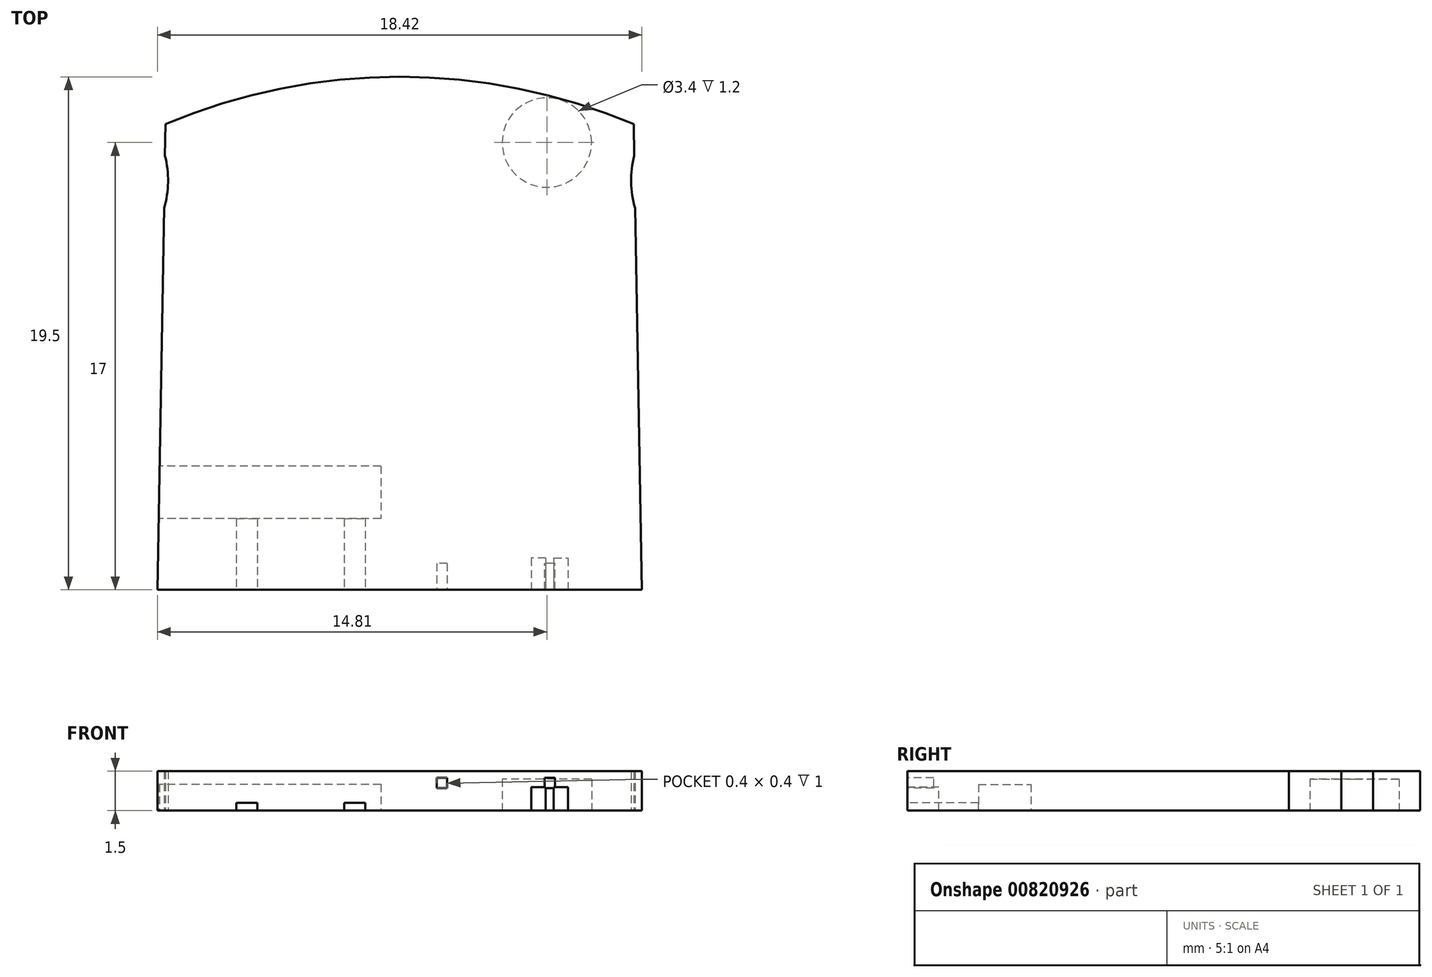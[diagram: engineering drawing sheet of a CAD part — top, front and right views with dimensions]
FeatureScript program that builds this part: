
annotation { "Feature Type Name" : "Feature", "Feature Type Description" : "" }
export const myFeature = defineFeature(function(context is Context, id is Id, definition is map)
    precondition{}
    {
        {
            var Q0;
            Q0=qCreatedBy(makeId("Top.planeOp"),FACE);
            var sketch = newSketch(context, id + "F0", { "sketchPlane" : qUnion([Q0])});
            skLineSegment(sketch, "E0", {"start": v(-9.2, 0) * mm, "end": v(9.21, 0) * mm});
            skLineSegment(sketch, "E1", {"start": v(-9.21, 0) * mm, "end": v(-8.9, 17.7) * mm});
            skLineSegment(sketch, "E2", {"start": v(-8.9, 17.7) * mm, "end": v(8.9, 17.7) * mm});
            skLineSegment(sketch, "E3", {"start": v(8.9, 17.7) * mm, "end": v(9.21, 0) * mm});
            skPoint(sketch, "E4", {"position": v(0, 19.5) * mm});
            skArc(sketch, "E5", {"start": v(8.9, 17.7) * mm, "mid": v(0, 19.5) * mm, "end": v(-8.9, 17.7) * mm});
            skPoint(sketch, "E6", {"position": v(-8.96, 14.5) * mm});
            skPoint(sketch, "E7", {"position": v(-8.92, 16.5) * mm});
            skPoint(sketch, "E8", {"position": v(-8.8, 15.5) * mm});
            skArc(sketch, "E9", {"start": v(-8.96, 14.5) * mm, "mid": v(-8.8, 15.5) * mm, "end": v(-8.92, 16.5) * mm});
            skArc(sketch, "E10.MirrorCS", {"start": v(8.96, 14.5) * mm, "mid": v(8.8, 15.5) * mm, "end": v(8.92, 16.5) * mm});
            skSolve(sketch);
        }
        {
            var Q0;
            {var subQ4=sQuery(id+"F0.wireOp",EDGE,"E0");Q0=makeQuery(id+"F0.imprint","IMPRINT",FACE,{"disambiguationData":[TD([[makeQuery(id+"F0.imprint","IMPRINT",EDGE,{"derivedFrom":subQ4}),1.0]])]});}
            var Q1;
            Q1=makeQuery(id+"F0.imprint","IMPRINT",FACE,{"disambiguationData":[TD([[makeQuery(id+"F0.imprint","IMPRINT",EDGE,{"derivedFrom":sQuery(id+"F0.wireOp",EDGE,"E2")}),1.0]])]});
            extrude(context, id + "F1", {"entities" : qUnion([Q0, Q1]), "depth" : 1.5 * mm, "offsetDistance" : 25 * mm});
        }
        {
            var Q0;
            Q0=qCreatedBy(makeId("Top.planeOp"),FACE);
            var sketch = newSketch(context, id + "F2", { "sketchPlane" : qUnion([Q0])});
            skLineSegment(sketch, "E11", {"start": v(5.6, 21.02) * mm, "end": v(5.6, -2.21) * mm, "construction": true});
            skLineSegment(sketch, "E12", {"start": v(13.66, 17) * mm, "end": v(-14.4, 17) * mm, "construction": true});
            skCircle(sketch, "E13", {"center": v(5.6, 17) * mm, "radius": 1.7 * mm});
            skCircle(sketch, "E14.MirrorC", {"center": v(-5.6, 17) * mm, "radius": 1.7 * mm});
            skSolve(sketch);
        }
        {
            var Q0;
            Q0=makeQuery(id+"F2.imprint","IMPRINT",FACE,{"disambiguationData":[TD([[makeQuery(id+"F2.imprint","IMPRINT",EDGE,{"derivedFrom":sQuery(id+"F2.wireOp",EDGE,"E13")}),1.0]])]});
            var Q1;
            Q1=makeQuery(id+"F2.imprint","IMPRINT",FACE,{"disambiguationData":[TD([[makeQuery(id+"F2.imprint","IMPRINT",EDGE,{"derivedFrom":sQuery(id+"F2.wireOp",EDGE,"E14.MirrorC")}),-1.0]])]});
            extrude(context, id + "F3", {"entities" : qUnion([Q0, Q1]), "operationType" : NewBodyOperationType.REMOVE, "depth" : 1.2 * mm, "offsetDistance" : 25 * mm});
        }
        {
            var Q0;
            Q0=makeQuery(id+"F1.opExtrude","CAP_FACE",FACE,{"disambiguationData":[OSD([sQuery(id+"F0.wireOp",EDGE,"E0"),sQuery(id+"F0.wireOp",EDGE,"E1"),sQuery(id+"F0.wireOp",EDGE,"E3"),sQuery(id+"F0.wireOp",EDGE,"E5"),sQuery(id+"F0.wireOp",EDGE,"E9"),sQuery(id+"F0.wireOp",EDGE,"E10.MirrorCS")])],"isStart":true});
            var sketch = newSketch(context, id + "F4", { "sketchPlane" : qUnion([Q0])});
            skLineSegment(sketch, "E15", {"start": v(9.68, -4.7) * mm, "end": v(-12.52, -4.7) * mm});
            skLineSegment(sketch, "E16", {"start": v(9.86, -2.7) * mm, "end": v(-11.55, -2.7) * mm});
            skLineSegment(sketch, "E17", {"start": v(-0.7, -9.35) * mm, "end": v(-0.7, 2.72) * mm});
            skLineSegment(sketch, "E18", {"start": v(-9.2, 0) * mm, "end": v(-9.2, -15.18) * mm});
            skSolve(sketch);
        }
        {
            var Q0;
            {var subQ0=sQuery(id+"F4.wireOp",EDGE,"E17");var subQ1=sQuery(id+"F4.wireOp",EDGE,"E15");var subQ2=makeQuery(id+"F4.imprint","INTERSECT",VERTEX,{"derivedFrom":[subQ1,subQ0]});Q0=makeQuery(id+"F4.imprint","IMPRINT",FACE,{"disambiguationData":[TD([[makeQuery(id+"F4.imprint","IMPRINT",EDGE,{"disambiguationData":[TD([[subQ2,-1.0]])],"derivedFrom":subQ0}),1.0]])]});}
            extrude(context, id + "F5", {"entities" : qUnion([Q0]), "operationType" : NewBodyOperationType.REMOVE, "oppositeDirection" : true, "depth" : 1 * mm, "offsetDistance" : 25 * mm});
        }
        {
            var Q0;
            Q0=makeQuery(id+"F1.opExtrude","CAP_FACE",FACE,{"disambiguationData":[OSD([sQuery(id+"F0.wireOp",EDGE,"E0"),sQuery(id+"F0.wireOp",EDGE,"E1"),sQuery(id+"F0.wireOp",EDGE,"E3"),sQuery(id+"F0.wireOp",EDGE,"E5"),sQuery(id+"F0.wireOp",EDGE,"E9"),sQuery(id+"F0.wireOp",EDGE,"E10.MirrorCS")])],"isStart":true});
            var sketch = newSketch(context, id + "F6", { "sketchPlane" : qUnion([Q0])});
            skLineSegment(sketch, "E19", {"start": v(-1.7, -5.79) * mm, "end": v(-1.71, 3.18) * mm, "construction": true});
            skLineSegment(sketch, "E20", {"start": v(-5.8, -6) * mm, "end": v(-5.81, 2.5) * mm, "construction": true});
            skLineSegment(sketch, "E21", {"start": v(13.46, -1.75) * mm, "end": v(-21.1, -1.75) * mm, "construction": true});
            skLineSegment(sketch, "E22.bottom", {"start": v(-1.31, -3.75) * mm, "end": v(-2.1, -3.75) * mm});
            skLineSegment(sketch, "E22.top", {"start": v(-1.3, 0.25) * mm, "end": v(-2.1, 0.25) * mm});
            skLineSegment(sketch, "E22.left", {"start": v(-1.3, -3.75) * mm, "end": v(-1.31, 0.25) * mm});
            skLineSegment(sketch, "E22.right", {"start": v(-2.1, -3.75) * mm, "end": v(-2.1, 0.25) * mm});
            skPoint(sketch, "E22.middle", {"position": v(-1.7, -1.75) * mm});
            skLineSegment(sketch, "E23.bottom", {"start": v(-5.4, -3.75) * mm, "end": v(-6.2, -3.75) * mm});
            skLineSegment(sketch, "E23.top", {"start": v(-5.4, 0.25) * mm, "end": v(-6.2, 0.25) * mm});
            skLineSegment(sketch, "E23.left", {"start": v(-5.4, -3.75) * mm, "end": v(-5.4, 0.25) * mm});
            skLineSegment(sketch, "E23.right", {"start": v(-6.2, -3.75) * mm, "end": v(-6.2, 0.25) * mm});
            skPoint(sketch, "E23.middle", {"position": v(-5.8, -1.75) * mm});
            skSolve(sketch);
        }
        {
            var Q0;
            {var subQ0=sQuery(id+"F6.wireOp",EDGE,"E22.left");var subQ1=makeQuery(id+"F5.boolean.opBoolean","COPY",EDGE,{"derivedFrom":makeQuery(id+"F5.opExtrude","CAP_EDGE",EDGE,{"disambiguationData":[OSD([sQuery(id+"F4.wireOp",EDGE,"E16")])],"isStart":true})});var subQ2=makeQuery(id+"F6.imprint","INTERSECT",VERTEX,{"derivedFrom":[subQ1,subQ0]});Q0=makeQuery(id+"F6.imprint","IMPRINT",FACE,{"disambiguationData":[TD([[makeQuery(id+"F6.imprint","IMPRINT",EDGE,{"disambiguationData":[TD([[subQ2,-1.0]])],"derivedFrom":subQ0}),1.0]])]});}
            var Q1;
            {var subQ0=sQuery(id+"F6.wireOp",EDGE,"E23.left");var subQ1=makeQuery(id+"F5.boolean.opBoolean","COPY",EDGE,{"derivedFrom":makeQuery(id+"F5.opExtrude","CAP_EDGE",EDGE,{"disambiguationData":[OSD([sQuery(id+"F4.wireOp",EDGE,"E16")])],"isStart":true})});var subQ2=makeQuery(id+"F6.imprint","INTERSECT",VERTEX,{"derivedFrom":[subQ1,subQ0]});Q1=makeQuery(id+"F6.imprint","IMPRINT",FACE,{"disambiguationData":[TD([[makeQuery(id+"F6.imprint","IMPRINT",EDGE,{"disambiguationData":[TD([[subQ2,-1.0]])],"derivedFrom":subQ0}),1.0]])]});}
            extrude(context, id + "F7", {"entities" : qUnion([Q0, Q1]), "operationType" : NewBodyOperationType.REMOVE, "oppositeDirection" : true, "depth" : 0.3 * mm, "offsetDistance" : 25 * mm});
        }
        {
            var Q0;
            Q0=makeQuery(id+"F1.opExtrude","SWEPT_FACE",FACE,{"disambiguationData":[OSD([sQuery(id+"F0.wireOp",EDGE,"E0")])]});
            var sketch = newSketch(context, id + "F8", { "sketchPlane" : qUnion([Q0])});
            skLineSegment(sketch, "E24", {"start": v(5.71, -2.14) * mm, "end": v(5.71, 4.32) * mm, "construction": true});
            skLineSegment(sketch, "E25", {"start": v(1.61, -2.11) * mm, "end": v(1.61, 4.26) * mm, "construction": true});
            skLineSegment(sketch, "E26.0", {"start": v(-1.3, 0) * mm, "end": v(9.21, 0) * mm});
            skLineSegment(sketch, "E27", {"start": v(9.7, 0.9) * mm, "end": v(0.57, 0.9) * mm});
            skLineSegment(sketch, "E28", {"start": v(5.86, 0) * mm, "end": v(5.86, 1.2) * mm});
            skLineSegment(sketch, "E29", {"start": v(6.41, 0) * mm, "end": v(6.41, 0.9) * mm});
            skLineSegment(sketch, "E30", {"start": v(5.56, 0) * mm, "end": v(5.56, 1.2) * mm});
            skLineSegment(sketch, "E31", {"start": v(5.01, 0) * mm, "end": v(5.01, 0.9) * mm});
            skLineSegment(sketch, "E32", {"start": v(9.67, 1.2) * mm, "end": v(2.64, 1.2) * mm});
            skLineSegment(sketch, "E33.bottom", {"start": v(2.31, 0) * mm, "end": v(1.76, 0) * mm});
            skLineSegment(sketch, "E33.top", {"start": v(2.31, 0.9) * mm, "end": v(1.76, 0.9) * mm});
            skLineSegment(sketch, "E33.left", {"start": v(2.31, 0) * mm, "end": v(2.31, 0.9) * mm});
            skLineSegment(sketch, "E33.right", {"start": v(1.76, 0) * mm, "end": v(1.76, 0.9) * mm});
            skLineSegment(sketch, "E34.bottom", {"start": v(1.46, 0) * mm, "end": v(0.91, 0) * mm});
            skLineSegment(sketch, "E34.top", {"start": v(1.46, 0.9) * mm, "end": v(0.91, 0.9) * mm});
            skLineSegment(sketch, "E34.left", {"start": v(1.46, 0) * mm, "end": v(1.46, 0.9) * mm});
            skLineSegment(sketch, "E34.right", {"start": v(0.91, 0) * mm, "end": v(0.91, 0.9) * mm});
            skSolve(sketch);
        }
        {
            var Q0;
            {var subQ3=sQuery(id+"F8.wireOp",EDGE,"E29");Q0=makeQuery(id+"F8.imprint","IMPRINT",FACE,{"disambiguationData":[TD([[makeQuery(id+"F8.imprint","IMPRINT",EDGE,{"derivedFrom":subQ3}),1.0]])]});}
            var Q1;
            {var subQ3=sQuery(id+"F8.wireOp",EDGE,"E31");Q1=makeQuery(id+"F8.imprint","IMPRINT",FACE,{"disambiguationData":[TD([[makeQuery(id+"F8.imprint","IMPRINT",EDGE,{"derivedFrom":subQ3}),-1.0]])]});}
            var Q2;
            Q2=makeQuery(id+"F8.imprint","IMPRINT",FACE,{"disambiguationData":[TD([[makeQuery(id+"F8.imprint","IMPRINT",EDGE,{"derivedFrom":sQuery(id+"F8.wireOp",EDGE,"E34.bottom")}),1.0]])]});
            var Q3;
            Q3=makeQuery(id+"F8.imprint","IMPRINT",FACE,{"disambiguationData":[TD([[makeQuery(id+"F8.imprint","IMPRINT",EDGE,{"derivedFrom":sQuery(id+"F8.wireOp",EDGE,"E33.bottom")}),1.0]])]});
            extrude(context, id + "F9", {"entities" : qUnion([Q0, Q1, Q2, Q3]), "operationType" : NewBodyOperationType.REMOVE, "oppositeDirection" : true, "depth" : 1.2 * mm, "offsetDistance" : 25 * mm});
        }
        {
            var Q0;
            Q0=makeQuery(id+"F1.opExtrude","SWEPT_FACE",FACE,{"disambiguationData":[OSD([sQuery(id+"F0.wireOp",EDGE,"E0")])]});
            var sketch = newSketch(context, id + "F10", { "sketchPlane" : qUnion([Q0])});
            skLineSegment(sketch, "E35", {"start": v(5.71, -2.14) * mm, "end": v(5.71, 4.32) * mm, "construction": true});
            skLineSegment(sketch, "E36", {"start": v(1.61, -2.11) * mm, "end": v(1.61, 4.26) * mm, "construction": true});
            skLineSegment(sketch, "E37.0", {"start": v(-1.3, 0) * mm, "end": v(9.21, 0) * mm});
            skLineSegment(sketch, "E38", {"start": v(9.7, 0.9) * mm, "end": v(6.41, 0.9) * mm});
            skLineSegment(sketch, "E39", {"start": v(5.86, 0.9) * mm, "end": v(5.86, 1.2) * mm});
            skLineSegment(sketch, "E40", {"start": v(6.41, 0) * mm, "end": v(6.41, 0.9) * mm});
            skLineSegment(sketch, "E41", {"start": v(5.56, 0.9) * mm, "end": v(5.56, 1.2) * mm});
            skLineSegment(sketch, "E42", {"start": v(5.01, 0) * mm, "end": v(5.01, 0.9) * mm});
            skLineSegment(sketch, "E43", {"start": v(5.86, 1.2) * mm, "end": v(5.56, 1.2) * mm});
            skLineSegment(sketch, "E44.bottom", {"start": v(2.31, 0) * mm, "end": v(1.76, 0) * mm});
            skLineSegment(sketch, "E44.left", {"start": v(2.31, 0) * mm, "end": v(2.31, 0.9) * mm});
            skLineSegment(sketch, "E44.right", {"start": v(1.76, 0.9) * mm, "end": v(1.76, 1.2) * mm});
            skLineSegment(sketch, "E45.bottom", {"start": v(1.46, 0) * mm, "end": v(0.91, 0) * mm});
            skLineSegment(sketch, "E45.left", {"start": v(1.46, 0.9) * mm, "end": v(1.46, 1.2) * mm});
            skLineSegment(sketch, "E45.right", {"start": v(0.91, 0) * mm, "end": v(0.91, 0.9) * mm});
            skPoint(sketch, "E46.orphan", {"position": v(5.86, 0) * mm});
            skPoint(sketch, "E47.orphan", {"position": v(5.56, 0) * mm});
            skLineSegment(sketch, "E48.trimOffspring", {"start": v(0.91, 0.9) * mm, "end": v(0.57, 0.9) * mm});
            skLineSegment(sketch, "E49.trimOffspring", {"start": v(1.76, 1.2) * mm, "end": v(1.46, 1.2) * mm});
            skPoint(sketch, "E50.orphan", {"position": v(0, 1.2) * mm});
            skLineSegment(sketch, "E51.trimOffspring", {"start": v(1.76, 0.9) * mm, "end": v(1.46, 0.9) * mm});
            skLineSegment(sketch, "E52.0", {"start": v(1.81, 0.85) * mm, "end": v(1.41, 0.85) * mm});
            skLineSegment(sketch, "E52.1", {"start": v(1.81, 0.85) * mm, "end": v(1.81, 1.25) * mm});
            skLineSegment(sketch, "E52.2", {"start": v(1.81, 1.25) * mm, "end": v(1.41, 1.25) * mm});
            skLineSegment(sketch, "E52.3", {"start": v(1.41, 0.85) * mm, "end": v(1.41, 1.25) * mm});
            skLineSegment(sketch, "E53.trimOffspring", {"start": v(5.86, 0.9) * mm, "end": v(5.56, 0.9) * mm});
            skLineSegment(sketch, "E54.trimOffspring", {"start": v(5.01, 0.9) * mm, "end": v(2.31, 0.9) * mm});
            skLineSegment(sketch, "E55.0", {"start": v(5.91, 0.85) * mm, "end": v(5.51, 0.85) * mm});
            skLineSegment(sketch, "E55.1", {"start": v(5.91, 0.85) * mm, "end": v(5.91, 1.25) * mm});
            skLineSegment(sketch, "E55.2", {"start": v(5.91, 1.25) * mm, "end": v(5.51, 1.25) * mm});
            skLineSegment(sketch, "E55.3", {"start": v(5.51, 0.85) * mm, "end": v(5.51, 1.25) * mm});
            skSolve(sketch);
        }
        {
            var Q0;
            Q0=makeQuery(id+"F10.imprint","IMPRINT",FACE,{"disambiguationData":[TD([[makeQuery(id+"F10.imprint","IMPRINT",EDGE,{"derivedFrom":sQuery(id+"F10.wireOp",EDGE,"E44.right")}),1.0]])]});
            var Q1;
            {var subQ0=sQuery(id+"F10.wireOp",EDGE,"E52.1");var subQ1=sQuery(id+"F10.wireOp",EDGE,"E52.0");var subQ2=makeQuery(id+"F10.imprint","INTERSECT",VERTEX,{"derivedFrom":[subQ1,subQ0]});Q1=makeQuery(id+"F10.imprint","IMPRINT",FACE,{"disambiguationData":[TD([[makeQuery(id+"F10.imprint","IMPRINT",EDGE,{"disambiguationData":[TD([[subQ2,-1.0]])],"derivedFrom":subQ1}),-1.0]])]});}
            var Q2;
            {var subQ0=sQuery(id+"F10.wireOp",EDGE,"E51.trimOffspring");Q2=makeQuery(id+"F10.imprint","IMPRINT",FACE,{"disambiguationData":[TD([[makeQuery(id+"F10.imprint","IMPRINT",EDGE,{"derivedFrom":subQ0}),1.0]])]});}
            var Q3;
            {var subQ0=sQuery(id+"F10.wireOp",EDGE,"E52.3");var subQ1=sQuery(id+"F10.wireOp",EDGE,"E52.0");var subQ2=makeQuery(id+"F10.imprint","INTERSECT",VERTEX,{"derivedFrom":[subQ1,subQ0]});Q3=makeQuery(id+"F10.imprint","IMPRINT",FACE,{"disambiguationData":[TD([[makeQuery(id+"F10.imprint","IMPRINT",EDGE,{"disambiguationData":[TD([[subQ2,1.0]])],"derivedFrom":subQ1}),-1.0]])]});}
            var Q4;
            {var subQ8=sQuery(id+"F10.wireOp",EDGE,"E44.right");Q4=makeQuery(id+"F10.imprint","IMPRINT",FACE,{"disambiguationData":[TD([[makeQuery(id+"F10.imprint","IMPRINT",EDGE,{"derivedFrom":subQ8}),-1.0]])]});}
            var Q5;
            {var subQ12=sQuery(id+"F10.wireOp",EDGE,"E39");Q5=makeQuery(id+"F10.imprint","IMPRINT",FACE,{"disambiguationData":[TD([[makeQuery(id+"F10.imprint","IMPRINT",EDGE,{"derivedFrom":subQ12}),-1.0]])]});}
            var Q6;
            Q6=makeQuery(id+"F10.imprint","IMPRINT",FACE,{"disambiguationData":[TD([[makeQuery(id+"F10.imprint","IMPRINT",EDGE,{"derivedFrom":sQuery(id+"F10.wireOp",EDGE,"E39")}),1.0]])]});
            var Q7;
            {var subQ0=sQuery(id+"F10.wireOp",EDGE,"E53.trimOffspring");Q7=makeQuery(id+"F10.imprint","IMPRINT",FACE,{"disambiguationData":[TD([[makeQuery(id+"F10.imprint","IMPRINT",EDGE,{"derivedFrom":subQ0}),1.0]])]});}
            var Q8;
            {var subQ0=sQuery(id+"F10.wireOp",EDGE,"E55.1");var subQ1=sQuery(id+"F10.wireOp",EDGE,"E55.0");var subQ2=makeQuery(id+"F10.imprint","INTERSECT",VERTEX,{"derivedFrom":[subQ1,subQ0]});Q8=makeQuery(id+"F10.imprint","IMPRINT",FACE,{"disambiguationData":[TD([[makeQuery(id+"F10.imprint","IMPRINT",EDGE,{"disambiguationData":[TD([[subQ2,-1.0]])],"derivedFrom":subQ1}),-1.0]])]});}
            var Q9;
            {var subQ0=sQuery(id+"F10.wireOp",EDGE,"E55.3");var subQ1=sQuery(id+"F10.wireOp",EDGE,"E55.0");var subQ2=makeQuery(id+"F10.imprint","INTERSECT",VERTEX,{"derivedFrom":[subQ1,subQ0]});Q9=makeQuery(id+"F10.imprint","IMPRINT",FACE,{"disambiguationData":[TD([[makeQuery(id+"F10.imprint","IMPRINT",EDGE,{"disambiguationData":[TD([[subQ2,1.0]])],"derivedFrom":subQ1}),-1.0]])]});}
            extrude(context, id + "F11", {"entities" : qUnion([Q0, Q1, Q2, Q3, Q4, Q5, Q6, Q7, Q8, Q9]), "operationType" : NewBodyOperationType.REMOVE, "oppositeDirection" : true, "depth" : 1 * mm, "offsetDistance" : 25 * mm});
        }
    });
